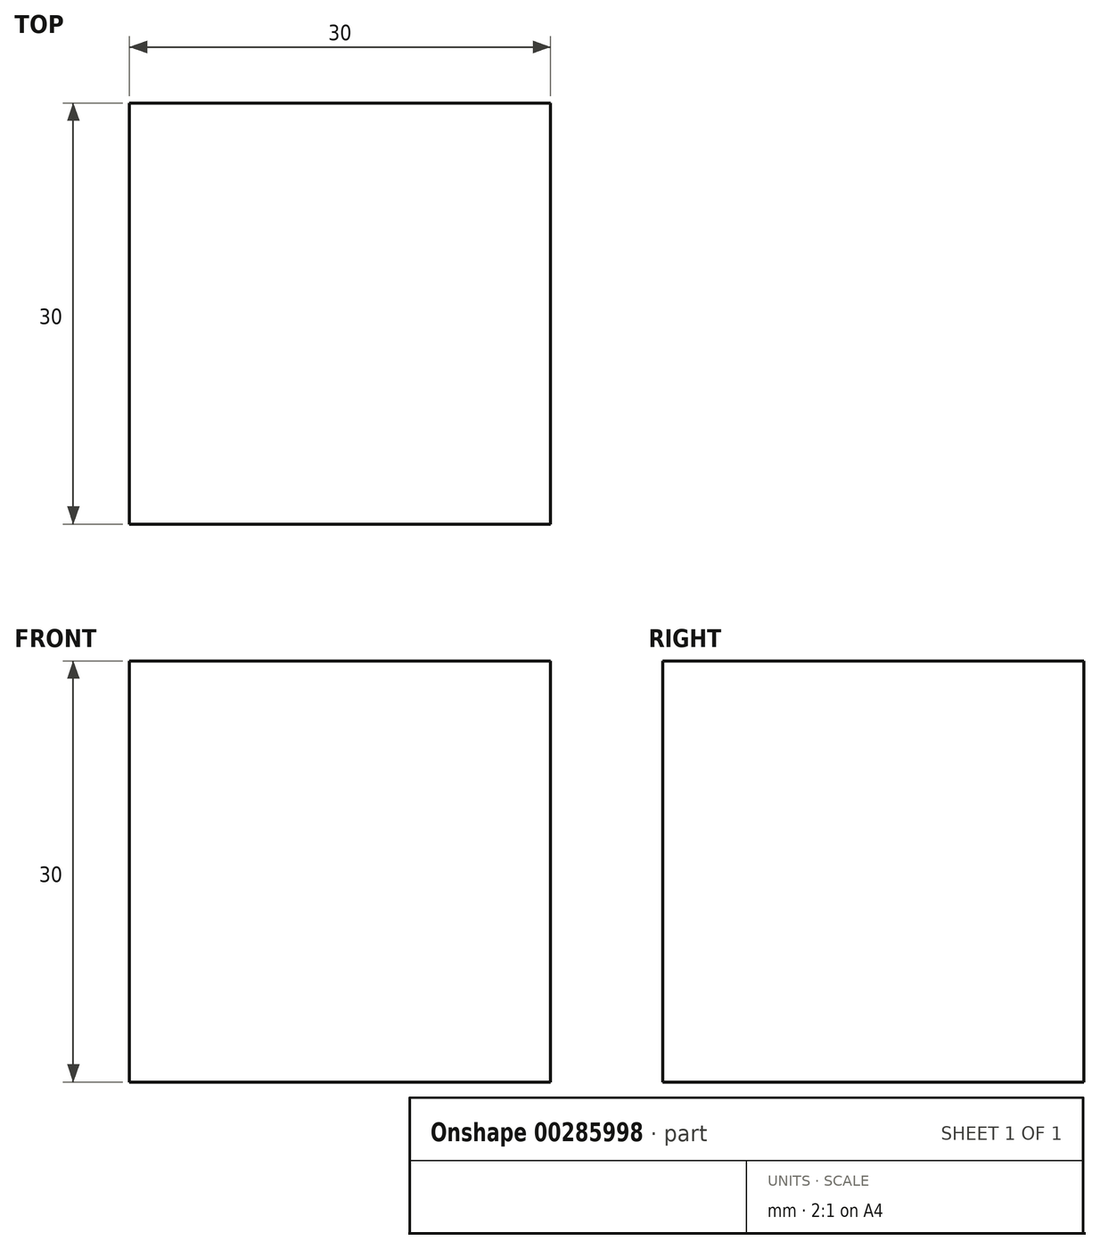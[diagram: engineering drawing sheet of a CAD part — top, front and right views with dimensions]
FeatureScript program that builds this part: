
annotation { "Feature Type Name" : "Feature", "Feature Type Description" : "" }
export const myFeature = defineFeature(function(context is Context, id is Id, definition is map)
    precondition{}
    {
        {
            var Q0;
            Q0=qCreatedBy(makeId("Front.planeOp"),FACE);
            var sketch = newSketch(context, id + "F0", { "sketchPlane" : qUnion([Q0])});
            skLineSegment(sketch, "E0.bottom", {"start": v(0, 0) * mm, "end": v(30, 0) * mm});
            skLineSegment(sketch, "E0.top", {"start": v(0, 30) * mm, "end": v(30, 30) * mm});
            skLineSegment(sketch, "E0.left", {"start": v(0, 0) * mm, "end": v(0, 30) * mm});
            skLineSegment(sketch, "E0.right", {"start": v(30, 0) * mm, "end": v(30, 30) * mm});
            skSolve(sketch);
        }
        {
            var Q0;
            Q0=makeQuery(id+"F0.imprint","IMPRINT",FACE,{"disambiguationData":[TD([[makeQuery(id+"F0.imprint","IMPRINT",EDGE,{"derivedFrom":sQuery(id+"F0.wireOp",EDGE,"E0.bottom")}),1.0]])]});
            extrude(context, id + "F1", {"entities" : qUnion([Q0]), "depth" : 30 * mm});
        }
    });
